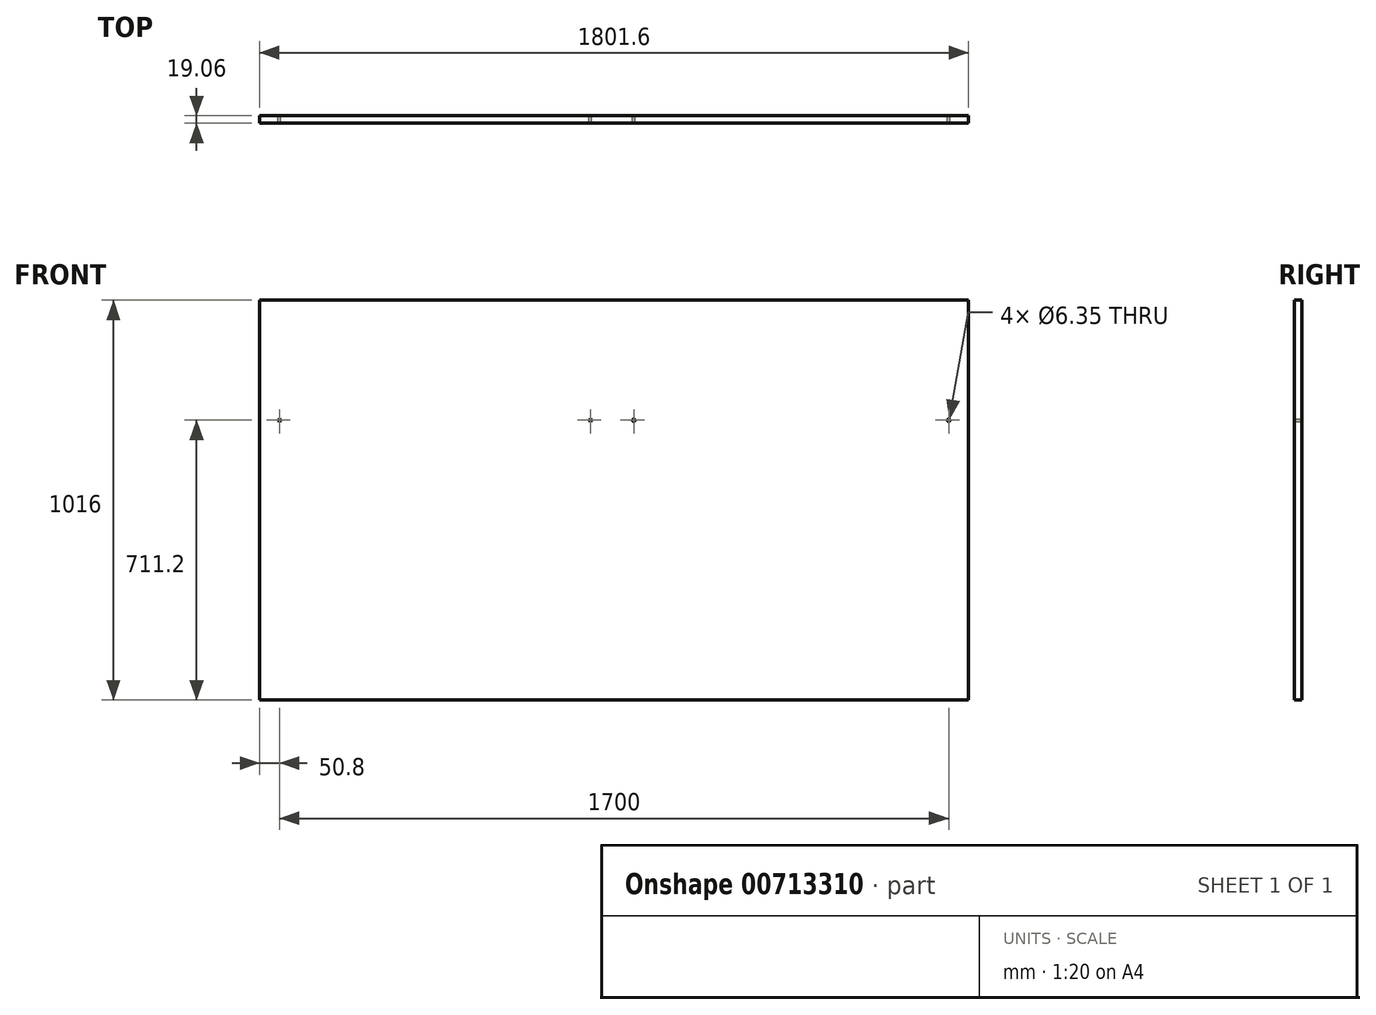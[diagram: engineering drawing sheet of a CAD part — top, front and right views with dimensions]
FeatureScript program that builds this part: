
annotation { "Feature Type Name" : "Feature", "Feature Type Description" : "" }
export const myFeature = defineFeature(function(context is Context, id is Id, definition is map)
    precondition{}
    {
        {
            var Q0;
            Q0=qCreatedBy(makeId("Front.planeOp"),FACE);
            var sketch = newSketch(context, id + "F0", { "sketchPlane" : qUnion([Q0])});
            skLineSegment(sketch, "E0.bottom", {"start": v(900.8, -508) * mm, "end": v(-900.8, -508) * mm});
            skLineSegment(sketch, "E0.top", {"start": v(900.8, 508) * mm, "end": v(-900.8, 508) * mm});
            skLineSegment(sketch, "E0.left", {"start": v(900.8, -508) * mm, "end": v(900.8, 508) * mm});
            skLineSegment(sketch, "E0.right", {"start": v(-900.8, -508) * mm, "end": v(-900.8, 508) * mm});
            skPoint(sketch, "E0.middle", {"position": v(0, 0) * mm});
            skCircle(sketch, "E1", {"center": v(-850, 203.2) * mm, "radius": 3.18 * mm});
            skCircle(sketch, "E2", {"center": v(-60, 203.2) * mm, "radius": 3.18 * mm});
            skCircle(sketch, "E3", {"center": v(50, 203.2) * mm, "radius": 3.18 * mm});
            skCircle(sketch, "E4", {"center": v(850, 203.2) * mm, "radius": 3.17 * mm});
            skSolve(sketch);
        }
        {
            var Q0;
            Q0=makeQuery(id+"F0.imprint","IMPRINT",FACE,{"disambiguationData":[TD([[makeQuery(id+"F0.imprint","IMPRINT",EDGE,{"derivedFrom":sQuery(id+"F0.wireOp",EDGE,"E0.bottom")}),-1.0]])]});
            extrude(context, id + "F1", {"entities" : qUnion([Q0]), "endBound" : BoundingType.SYMMETRIC, "depth" : 19.05 * mm, "offsetDistance" : 25.4 * mm});
        }
    });
